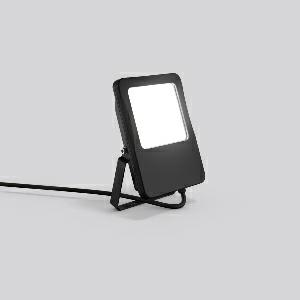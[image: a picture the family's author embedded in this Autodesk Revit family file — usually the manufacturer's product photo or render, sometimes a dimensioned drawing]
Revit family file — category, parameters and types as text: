
# Revit family: hb_450_722147_003_a05b
name_source: partatom
category: Lighting Fixtures
units: mm (PartAtom-declared; Revit-internal decimal feet)

## family parameters
Cut with Voids When Loaded = No
Host = Face
Light Source = No
Part Type = Normal
Room Calculation Point = No
Round Connector Dimension = Use Diameter
Shared = No

## types (1)
- HB 450 (1 x LED Modul 840, 5500 lm, 4000)
    Apparent Load = 50 VA
    CIE Flux Codes = 54 88 99 100 100
    Color Rendering = 80
    Color Temperature = 4000
    Default Elevation = 1800 mm
    Description = Series: HB 450
Projector for direct mains connection. Housing: die-cast aluminium, powder-coated. Bracket: steel, powder-coated. Clear glass cover. Wide flood. Pre-wired with 500 mm connection cable. 
Colour: black
Length: 195 mm
Width: 145 mm
Height: 41 mm
Lamp: LED
System power: 50 W
Rated luminous flux: 5500 lm
Luminous efficiency: 110 lm/W
Control gear: Regulated power supply
Protection class: I
Type of protection: IP 65
    Height = 41 mm
    Lamp = 1 x LED Modul 840
    Lamp Light Flux = 5500 lm
    Lamp count = 1
    Length = 195 mm
    Lifetime = 50000 h
    Luminous efficacy = 110 lm/W
    Manufacturer = RZB
    ModVariant = No
    Model = 722147.003
    Mounting Place = Floor
    Mounting Type = Surface mounted
    Number of Poles = 1
    OnlyDefault = Yes
    Power Factor = 1
    Product Name = HB 450
    Product group = Floodlights and spotlights
    ProductGroupID = 1354
    Protection Class = Protection class I
    Protection Degree = IP 65
    RLX_Detail_Level = 1
    RLX_Emergency_Light_Flux = 0 lm
    RLX_Emergency_Type = 0
    RLX_Emergency_Type_DB = No
    RlxData = <blob elided: 22601 chars, md5=69711a30>
    Socket = socket
    Standby Power = 0 W
    System Light Flux = 5500 lm
    System Power = 50 W
    Type Comments = Product without accessories
    Type Image = 722147.003.jpg
    URL = http://relux.com
    VarID = ---
    Voltage = 230 V
    Voltage Range = 220-240 V
    Weight = 0.00 kg
    Width = 145 mm

## geometry (parser evidence)
native form markers: Blend x4, Sweep x13
no freeform markers — native parametric forms only
